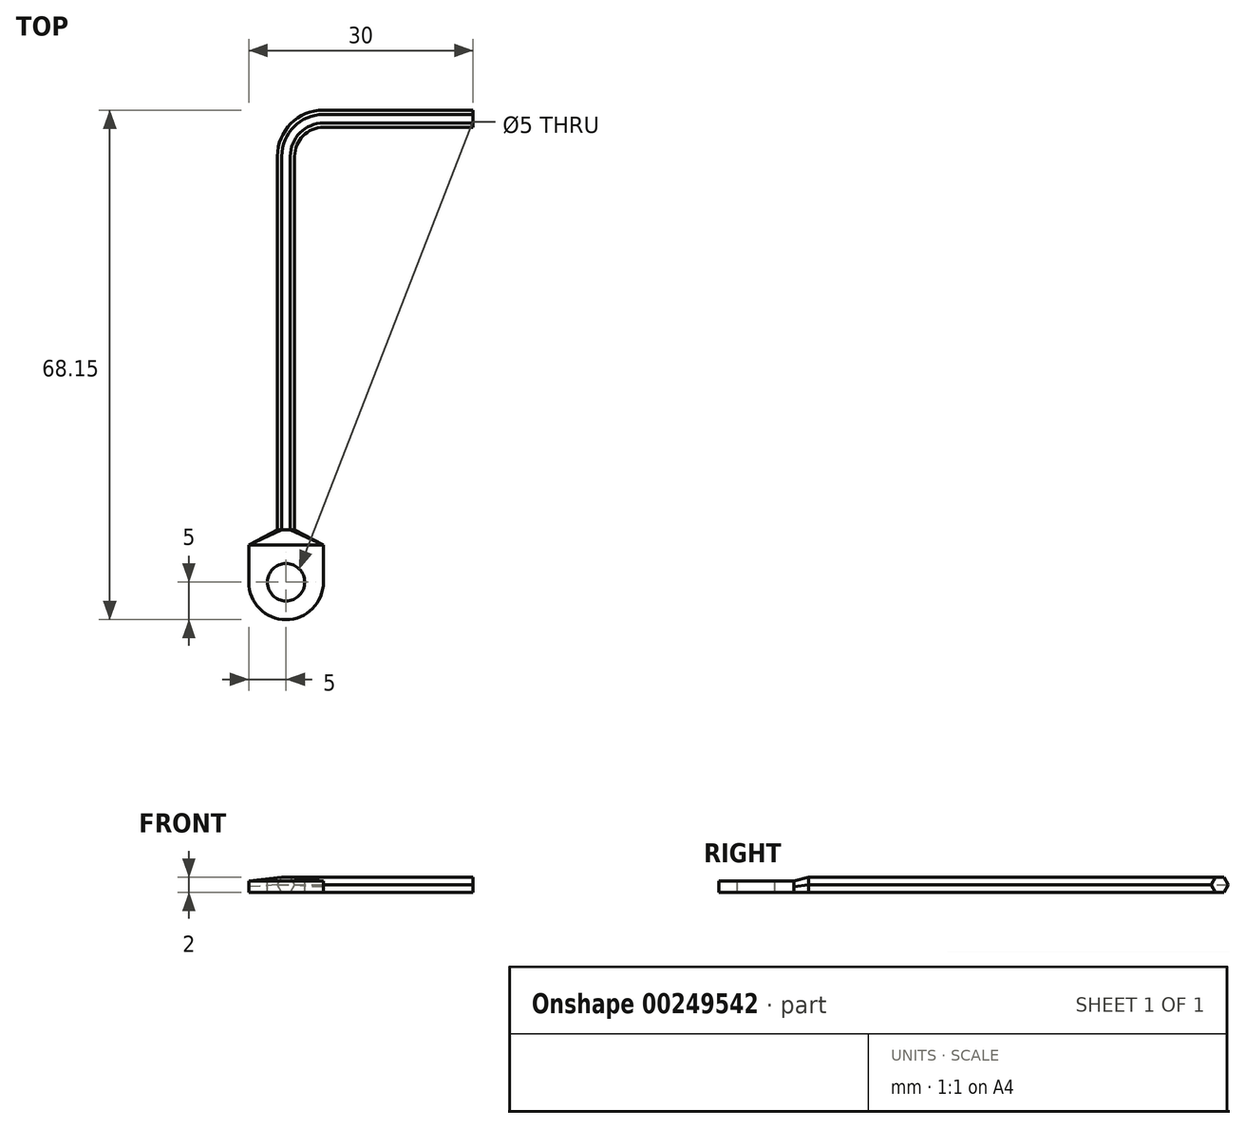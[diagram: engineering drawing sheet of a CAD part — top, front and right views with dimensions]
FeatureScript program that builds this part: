
annotation { "Feature Type Name" : "Feature", "Feature Type Description" : "" }
export const myFeature = defineFeature(function(context is Context, id is Id, definition is map)
    precondition{}
    {
        {
            var Q0;
            Q0=qCreatedBy(makeId("Front.planeOp"),FACE);
            var sketch = newSketch(context, id + "F0", { "sketchPlane" : qUnion([Q0])});
            skCircle(sketch, "E0.cCircle", {"center": v(0, 0) * mm, "radius": 1 * mm, "construction": true});
            skLineSegment(sketch, "E0.0", {"start": v(0.58, -1) * mm, "end": v(-0.58, -1) * mm});
            skLineSegment(sketch, "E0.1", {"start": v(-0.58, -1) * mm, "end": v(-1.15, 0) * mm});
            skLineSegment(sketch, "E0.2", {"start": v(-1.15, 0) * mm, "end": v(-0.58, 1) * mm});
            skLineSegment(sketch, "E0.3", {"start": v(-0.58, 1) * mm, "end": v(0.58, 1) * mm});
            skLineSegment(sketch, "E0.4", {"start": v(0.58, 1) * mm, "end": v(1.15, 0) * mm});
            skLineSegment(sketch, "E0.5", {"start": v(1.15, 0) * mm, "end": v(0.58, -1) * mm});
            skPoint(sketch, "E0.0.midPoint", {"position": v(0, -1) * mm});
            skSolve(sketch);
        }
        {
            var Q0;
            Q0=qCreatedBy(makeId("Top.planeOp"),FACE);
            var sketch = newSketch(context, id + "F1", { "sketchPlane" : qUnion([Q0])});
            skLineSegment(sketch, "E1", {"start": v(0, 0) * mm, "end": v(0, 50) * mm});
            skLineSegment(sketch, "E2", {"start": v(5, 55) * mm, "end": v(25, 55) * mm});
            skPoint(sketch, "E3.visualSharp", {"position": v(0, 55) * mm});
            skArc(sketch, "E3.filletArc", {"start": v(5, 55) * mm, "mid": v(1.46, 53.54) * mm, "end": v(0, 50) * mm});
            skSolve(sketch);
        }
        {
            var Q0;
            Q0=qSketchRegion(id+"F0",true);
            var Q1;
            Q1=qConstructionFilter(qBodyType(qCreatedBy(id+"F1",EDGE),BodyType.WIRE),ConstructionObject.NO);
            sweep(context, id + "F2", {"profiles" : qUnion([Q0]), "path" : qUnion([Q1])});
        }
        {
            var Q0;
            Q0=makeQuery(id+"F2.opSweep","CAP_FACE",FACE,{"disambiguationData":[OSD([sQuery(id+"F0.wireOp",EDGE,"E0.0"),sQuery(id+"F0.wireOp",EDGE,"E0.1"),sQuery(id+"F0.wireOp",EDGE,"E0.2"),sQuery(id+"F0.wireOp",EDGE,"E0.3"),sQuery(id+"F0.wireOp",EDGE,"E0.4"),sQuery(id+"F0.wireOp",EDGE,"E0.5"),sQuery(id+"F1.wireOp",VERTEX,"E1.start")])],"isStart":true});
            cPlane(context, id + "F3", {"entities" : qUnion([Q0]), "cplaneType" : CPlaneType.OFFSET, "offset" : 2 * mm, "width" : 150 * mm, "height" : 150 * mm});
        }
        {
            var Q0;
            Q0=qCreatedBy(id+"F3.planeOp",FACE);
            var sketch = newSketch(context, id + "F4", { "sketchPlane" : qUnion([Q0])});
            skLineSegment(sketch, "E4.bottom", {"start": v(-5, 0.5) * mm, "end": v(5, 0.5) * mm});
            skLineSegment(sketch, "E4.top", {"start": v(-5, -1) * mm, "end": v(5, -1) * mm});
            skLineSegment(sketch, "E4.left", {"start": v(-5, 0.5) * mm, "end": v(-5, -1) * mm});
            skLineSegment(sketch, "E4.right", {"start": v(5, 0.5) * mm, "end": v(5, -1) * mm});
            skSolve(sketch);
        }
        {
            var Q0;
            Q0=qSketchRegion(id+"F4",true);
            extrude(context, id + "F5", {"entities" : qUnion([Q0]), "depth" : 10 * mm});
        }
        {
            var Q0;
            Q0=makeQuery(id+"F5.opExtrude","SWEPT_FACE",FACE,{"disambiguationData":[OSD([sQuery(id+"F4.wireOp",EDGE,"E4.bottom")])]});
            var sketch = newSketch(context, id + "F6", { "sketchPlane" : qUnion([Q0])});
            skCircle(sketch, "E5", {"center": v(0, -7) * mm, "radius": 2.5 * mm});
            skPoint(sketch, "E5.centerSnap0", {"position": v(-5, -7) * mm});
            skPoint(sketch, "E5.centerSnap1", {"position": v(0, -12) * mm});
            skSolve(sketch);
        }
        {
            var Q0;
            Q0=qSketchRegion(id+"F6",true);
            extrude(context, id + "F7", {"entities" : qUnion([Q0]), "operationType" : NewBodyOperationType.REMOVE, "oppositeDirection" : true, "depth" : 25 * mm});
        }
        {
            var Q0;
            Q0=makeQuery(id+"F5.opExtrude","CAP_FACE",FACE,{"disambiguationData":[OSD([sQuery(id+"F4.wireOp",EDGE,"E4.bottom"),sQuery(id+"F4.wireOp",EDGE,"E4.top"),sQuery(id+"F4.wireOp",EDGE,"E4.left"),sQuery(id+"F4.wireOp",EDGE,"E4.right")])],"isStart":true});
            var sketch = newSketch(context, id + "F8", { "sketchPlane" : qUnion([Q0])});
            skLineSegment(sketch, "E6", {"start": v(-5, 0.5) * mm, "end": v(5, 0.5) * mm});
            skLineSegment(sketch, "E7", {"start": v(5, 0.5) * mm, "end": v(5, -0.25) * mm});
            skLineSegment(sketch, "E8", {"start": v(5, -0.25) * mm, "end": v(5, -1) * mm});
            skLineSegment(sketch, "E9", {"start": v(5, -1) * mm, "end": v(-5, -1) * mm});
            skLineSegment(sketch, "E10", {"start": v(-5, -1) * mm, "end": v(-5, -0.25) * mm});
            skLineSegment(sketch, "E11", {"start": v(-5, -0.25) * mm, "end": v(-5, 0.5) * mm});
            skSolve(sketch);
        }
        {
            var Q0;
            Q0=makeQuery(id+"F2.opSweep","CAP_FACE",FACE,{"disambiguationData":[OSD([sQuery(id+"F0.wireOp",EDGE,"E0.0"),sQuery(id+"F0.wireOp",EDGE,"E0.1"),sQuery(id+"F0.wireOp",EDGE,"E0.2"),sQuery(id+"F0.wireOp",EDGE,"E0.3"),sQuery(id+"F0.wireOp",EDGE,"E0.4"),sQuery(id+"F0.wireOp",EDGE,"E0.5"),sQuery(id+"F1.wireOp",VERTEX,"E1.start")])],"isStart":true});
            var Q1;
            Q1=makeQuery(id+"F8.imprint","IMPRINT",FACE,{"disambiguationData":[TD([[makeQuery(id+"F8.imprint","IMPRINT",EDGE,{"derivedFrom":sQuery(id+"F8.wireOp",EDGE,"E6")}),1.0]])]});
            loft(context, id + "F9", {"sheetProfilesArray" : [{ "sheetProfileEntities" : qUnion([Q0]) }, { "sheetProfileEntities" : qUnion([Q1]) }]});
        }
        {
            var Q0;
            Q0=makeQuery(id+"F5.opExtrude","CAP_EDGE",EDGE,{"disambiguationData":[OSD([sQuery(id+"F4.wireOp",EDGE,"E4.right")])],"isStart":false});
            var Q1;
            Q1=makeQuery(id+"F5.opExtrude","CAP_EDGE",EDGE,{"disambiguationData":[OSD([sQuery(id+"F4.wireOp",EDGE,"E4.left")])],"isStart":false});
            fillet(context, id + "F10", {"entities" : qUnion([Q0, Q1]), "radius" : 5 * mm, "tangentPropagation" : true, "allowEdgeOverflow" : false});
        }
    });
